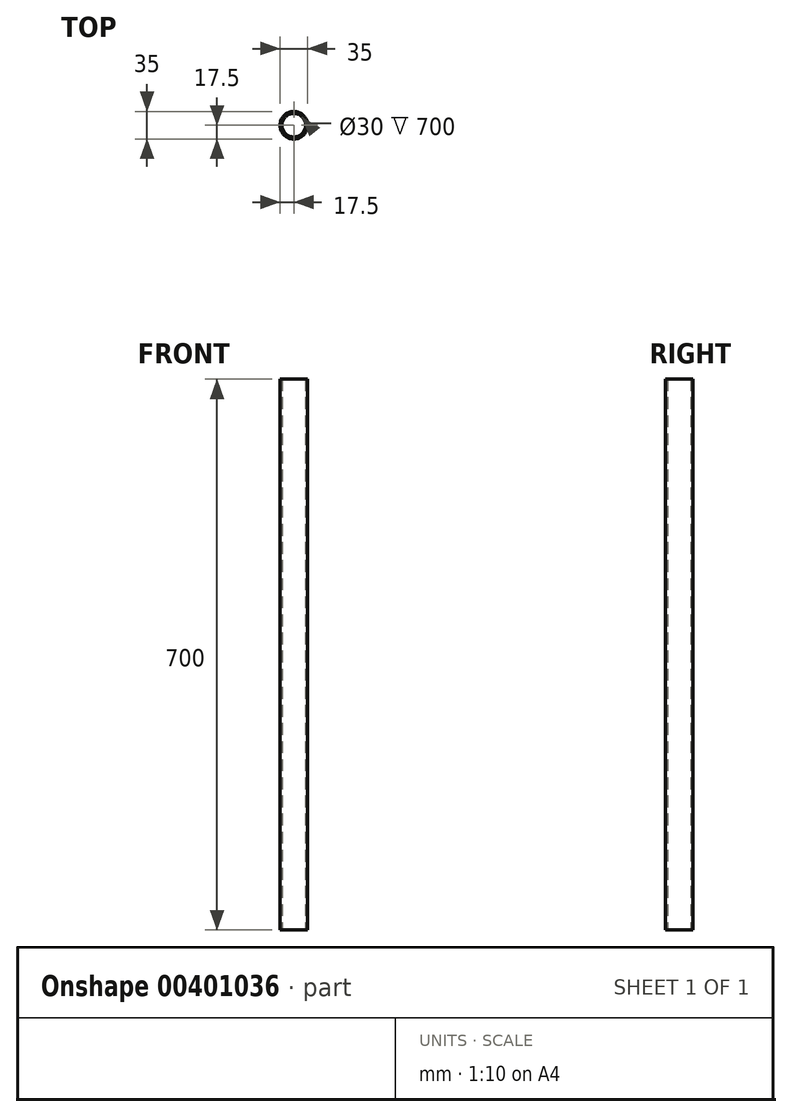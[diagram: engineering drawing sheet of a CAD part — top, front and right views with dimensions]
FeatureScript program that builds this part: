
annotation { "Feature Type Name" : "Feature", "Feature Type Description" : "" }
export const myFeature = defineFeature(function(context is Context, id is Id, definition is map)
    precondition{}
    {
        {
            var Q0;
            Q0=qCreatedBy(makeId("Top.planeOp"),FACE);
            var sketch = newSketch(context, id + "F0", { "sketchPlane" : qUnion([Q0])});
            skCircle(sketch, "E0", {"center": v(0, 0) * mm, "radius": 15 * mm});
            skCircle(sketch, "E1", {"center": v(0, 0) * mm, "radius": 17.5 * mm});
            skSolve(sketch);
        }
        {
            var Q0;
            Q0=makeQuery(id+"F0.imprint","IMPRINT",FACE,{"disambiguationData":[TD([[makeQuery(id+"F0.imprint","IMPRINT",EDGE,{"derivedFrom":sQuery(id+"F0.wireOp",EDGE,"E0")}),-1.0]])]});
            extrude(context, id + "F1", {"entities" : qUnion([Q0]), "depth" : 700 * mm});
        }
    });
